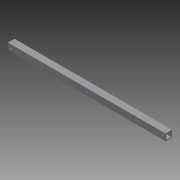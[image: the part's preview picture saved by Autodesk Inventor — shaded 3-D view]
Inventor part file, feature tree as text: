
AUTODESK INVENTOR PART (.ipt)
format: ipt  version: 2015 (Build 190159000, 159)  size: 108,544 bytes
history: native  units: in
note: dims shown in document units (in); Inventor stores cm internally (conversion verified against a paired STEP export)
features: sketch x3, extrude x2, projected_geometry x2, hole x1
ambient origin geometry x8: Origin, YZ Plane, XZ Plane, XY Plane, X Axis, Y Axis, Z Axis, Center Point
bodies: Solid1 (feature_tree)
feature tree (8):
  extrude  "Extrusion1"  Depth=1.0in
  hole  "Hole1"  [1 undecoded]
  extrude  "Extrusion2"  Depth=0.125in
  sketch  "Sketch1"  dims[d0=1.0in d1=1.0in]
  sketch  "Sketch2"  dims[d2=0.75in d3=0.75in]
  projected_geometry  "Projected Loop1"
  sketch  "Sketch3"  dims[d4=0.125in d5=0.125in d6=23.75in d7=0.0in d8=0.5in d9=0.5in d10=0.5in d11=0.5in d12=0.5in d13=11.875in d14=0.25in d15=0.75in d16=0.375in d17=0.25in d18=0.5635in d19=1.0in d20=0.8108in d21=0.625in d22=0.625in d23=0.625in d24=0.5in d25=0.0in]
  projected_geometry  "Projected Loop2"
note: 1 required parameter value undecoded (feature->parameter linkage not recoverable at this tier; creation-order binding heuristic only, values carry confidence <= 0.55)
